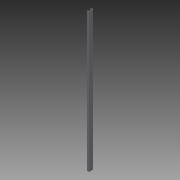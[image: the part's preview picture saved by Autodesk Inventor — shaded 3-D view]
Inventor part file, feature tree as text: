
AUTODESK INVENTOR PART (.ipt)
format: ipt  version: 2013 (Build 170138000, 138)  size: 79,360 bytes
history: native  units: in
note: dims shown in document units (in); Inventor stores cm internally (conversion verified against a paired STEP export)
features: other x2, extrude x1, sketch x1
ambient origin geometry x8: Origin, YZ Plane, XZ Plane, XY Plane, X Axis, Y Axis, Z Axis, Center Point
bodies: Solid1 (feature_tree)
feature tree (4):
  other  "Table"
  other  "cChannel2x1-01"
  extrude  "Extrusion1"  Depth=2.0in
  sketch  "Sketch1"  dims[d0=1.0in d1=2.0in d2=0.125in d3=0.125in d5=0.0in]
